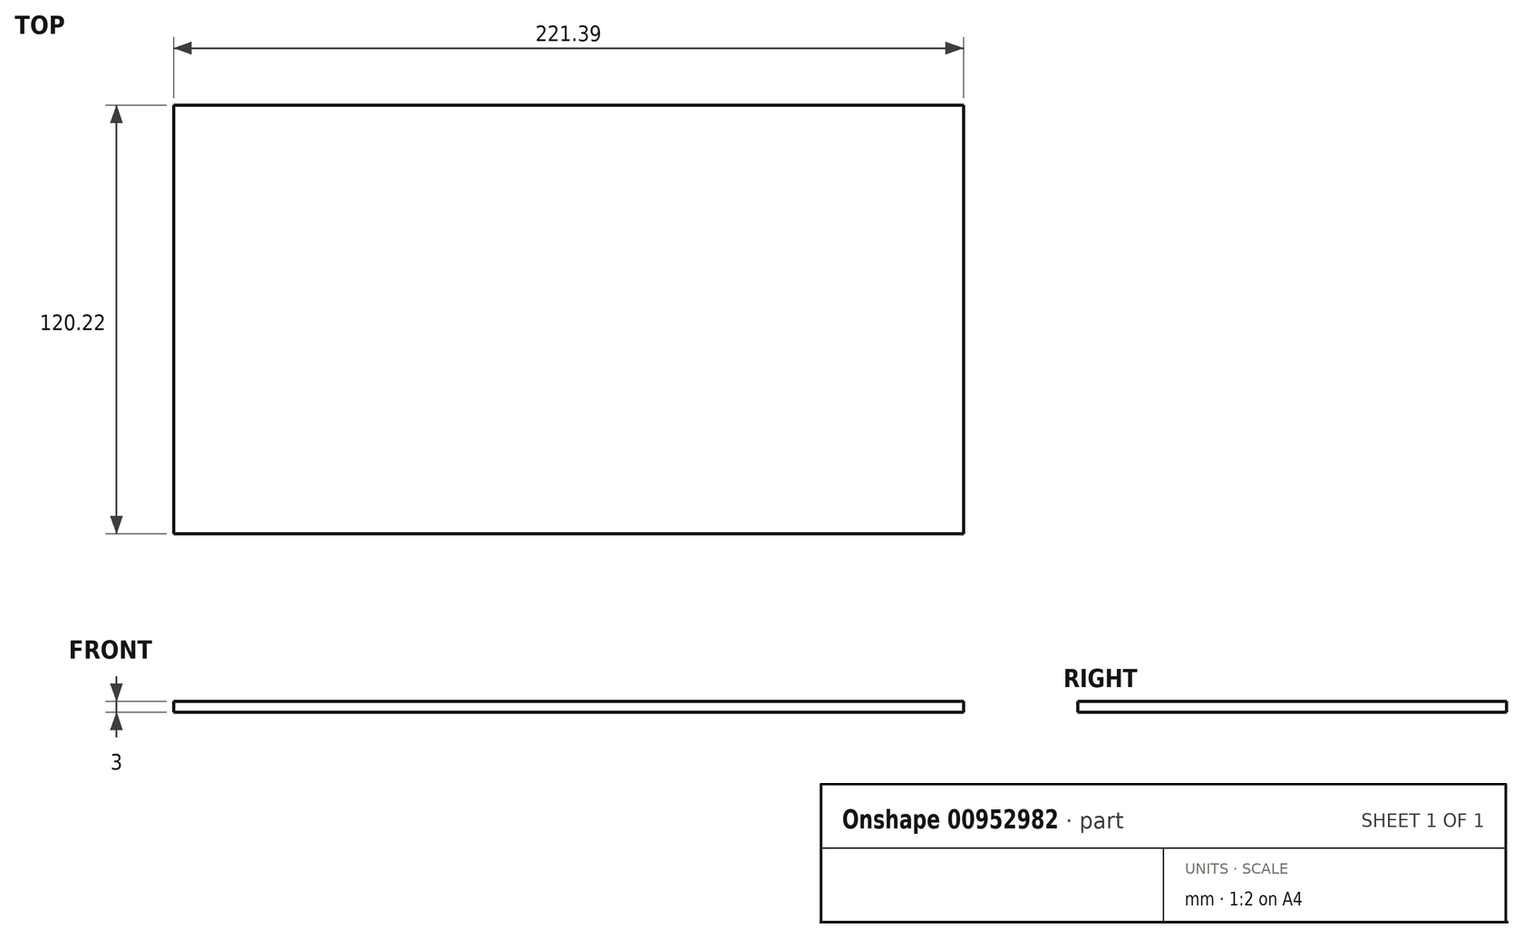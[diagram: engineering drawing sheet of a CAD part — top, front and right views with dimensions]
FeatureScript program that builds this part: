
annotation { "Feature Type Name" : "Feature", "Feature Type Description" : "" }
export const myFeature = defineFeature(function(context is Context, id is Id, definition is map)
    precondition{}
    {
        {
            var Q0;
            Q0=qCreatedBy(makeId("Top.planeOp"),FACE);
            var sketch = newSketch(context, id + "F0", { "sketchPlane" : qUnion([Q0])});
            skLineSegment(sketch, "E0.bottom", {"start": v(-135.52, 66.04) * mm, "end": v(85.87, 66.04) * mm});
            skLineSegment(sketch, "E0.top", {"start": v(-135.52, -54.18) * mm, "end": v(85.87, -54.18) * mm});
            skLineSegment(sketch, "E0.left", {"start": v(-135.52, 66.04) * mm, "end": v(-135.52, -54.18) * mm});
            skLineSegment(sketch, "E0.right", {"start": v(85.87, 66.04) * mm, "end": v(85.87, -54.18) * mm});
            skSolve(sketch);
        }
        {
            var Q0;
            Q0=makeQuery(id+"F0.imprint","IMPRINT",FACE,{"disambiguationData":[TD([[makeQuery(id+"F0.imprint","IMPRINT",EDGE,{"derivedFrom":sQuery(id+"F0.wireOp",EDGE,"E0.bottom")}),-1.0]])]});
            extrude(context, id + "F1", {"entities" : qUnion([Q0]), "depth" : 3 * mm, "offsetDistance" : 25 * mm});
        }
    });
